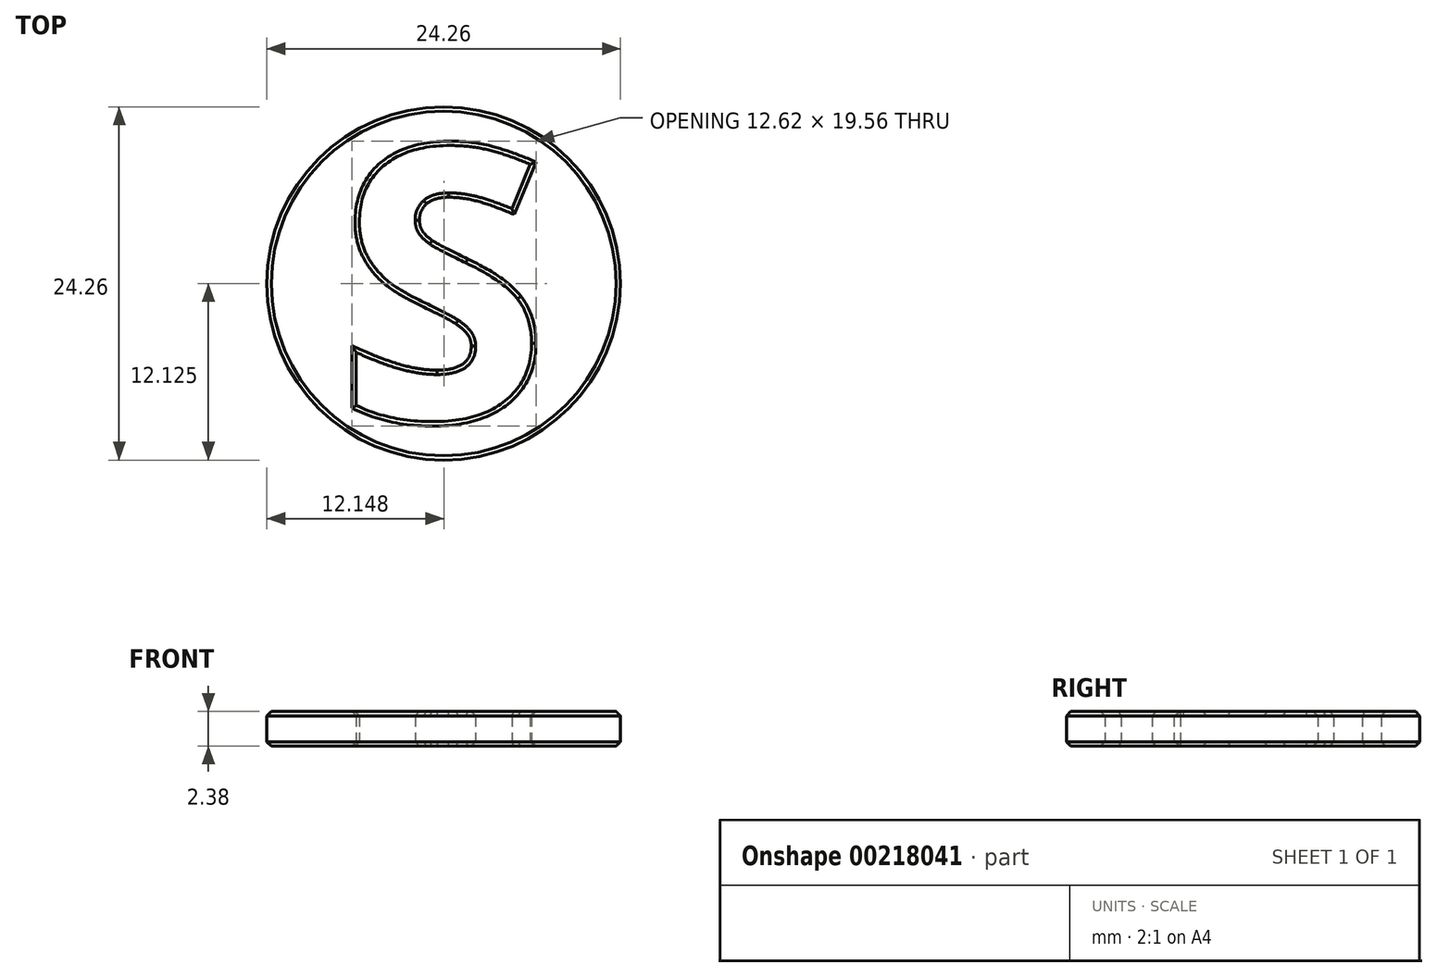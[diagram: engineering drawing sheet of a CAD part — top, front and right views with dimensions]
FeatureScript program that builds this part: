
annotation { "Feature Type Name" : "Feature", "Feature Type Description" : "" }
export const myFeature = defineFeature(function(context is Context, id is Id, definition is map)
    precondition{}
    {
        {
            var Q0;
            Q0=qCreatedBy(makeId("Top.planeOp"),FACE);
            var sketch = newSketch(context, id + "F0", { "sketchPlane" : qUnion([Q0])});
            skCircle(sketch, "E0", {"center": v(0, 0) * mm, "radius": 12.12 * mm});
            skText(sketch, "E1", { "text": "S", "fontName": "OpenSans-Bold.ttf"});
            const initialGuessF0  = {"E1": [-0.00718, -0.00923, 1, 0, 0.0186]};
            skSetInitialGuess(sketch, initialGuessF0);
            skSolve(sketch);
        }
        {
            var Q0;
            Q0=makeQuery(id+"F0.imprint","IMPRINT",FACE,{"disambiguationData":[TD([[makeQuery(id+"F0.imprint","IMPRINT",EDGE,{"derivedFrom":sQuery(id+"F0.wireOp",EDGE,"E0")}),1.0]])]});
            extrude(context, id + "F1", {"entities" : qUnion([Q0]), "depth" : 2.38 * mm});
        }
        {
            var Q0;
            Q0=makeQuery(id+"F1.opExtrude","CAP_FACE",FACE,{"disambiguationData":[OSD([sQuery(id+"F0.wireOp",EDGE,"E0"),sQuery(id+"F0.wireOp",EDGE,"E1.sketch_text.stroke-0"),sQuery(id+"F0.wireOp",EDGE,"E1.sketch_text.stroke-1"),sQuery(id+"F0.wireOp",EDGE,"E1.sketch_text.stroke-2"),sQuery(id+"F0.wireOp",EDGE,"E1.sketch_text.stroke-3"),sQuery(id+"F0.wireOp",EDGE,"E1.sketch_text.stroke-4"),sQuery(id+"F0.wireOp",EDGE,"E1.sketch_text.stroke-5"),sQuery(id+"F0.wireOp",EDGE,"E1.sketch_text.stroke-6"),sQuery(id+"F0.wireOp",EDGE,"E1.sketch_text.stroke-7"),sQuery(id+"F0.wireOp",EDGE,"E1.sketch_text.stroke-8"),sQuery(id+"F0.wireOp",EDGE,"E1.sketch_text.stroke-9"),sQuery(id+"F0.wireOp",EDGE,"E1.sketch_text.stroke-10"),sQuery(id+"F0.wireOp",EDGE,"E1.sketch_text.stroke-11"),sQuery(id+"F0.wireOp",EDGE,"E1.sketch_text.stroke-12"),sQuery(id+"F0.wireOp",EDGE,"E1.sketch_text.stroke-13"),sQuery(id+"F0.wireOp",EDGE,"E1.sketch_text.stroke-14"),sQuery(id+"F0.wireOp",EDGE,"E1.sketch_text.stroke-15"),sQuery(id+"F0.wireOp",EDGE,"E1.sketch_text.stroke-16"),sQuery(id+"F0.wireOp",EDGE,"E1.sketch_text.stroke-17"),sQuery(id+"F0.wireOp",EDGE,"E1.sketch_text.stroke-18"),sQuery(id+"F0.wireOp",EDGE,"E1.sketch_text.stroke-19"),sQuery(id+"F0.wireOp",EDGE,"E1.sketch_text.stroke-20"),sQuery(id+"F0.wireOp",EDGE,"E1.sketch_text.stroke-21"),sQuery(id+"F0.wireOp",EDGE,"E1.sketch_text.stroke-22"),sQuery(id+"F0.wireOp",EDGE,"E1.sketch_text.stroke-23"),sQuery(id+"F0.wireOp",EDGE,"E1.sketch_text.stroke-24"),sQuery(id+"F0.wireOp",EDGE,"E1.sketch_text.stroke-25"),sQuery(id+"F0.wireOp",EDGE,"E1.sketch_text.stroke-26"),sQuery(id+"F0.wireOp",EDGE,"E1.sketch_text.stroke-27")])],"isStart":false});
            var Q1;
            Q1=makeQuery(id+"F1.opExtrude","CAP_FACE",FACE,{"disambiguationData":[OSD([sQuery(id+"F0.wireOp",EDGE,"E0"),sQuery(id+"F0.wireOp",EDGE,"E1.sketch_text.stroke-0"),sQuery(id+"F0.wireOp",EDGE,"E1.sketch_text.stroke-1"),sQuery(id+"F0.wireOp",EDGE,"E1.sketch_text.stroke-2"),sQuery(id+"F0.wireOp",EDGE,"E1.sketch_text.stroke-3"),sQuery(id+"F0.wireOp",EDGE,"E1.sketch_text.stroke-4"),sQuery(id+"F0.wireOp",EDGE,"E1.sketch_text.stroke-5"),sQuery(id+"F0.wireOp",EDGE,"E1.sketch_text.stroke-6"),sQuery(id+"F0.wireOp",EDGE,"E1.sketch_text.stroke-7"),sQuery(id+"F0.wireOp",EDGE,"E1.sketch_text.stroke-8"),sQuery(id+"F0.wireOp",EDGE,"E1.sketch_text.stroke-9"),sQuery(id+"F0.wireOp",EDGE,"E1.sketch_text.stroke-10"),sQuery(id+"F0.wireOp",EDGE,"E1.sketch_text.stroke-11"),sQuery(id+"F0.wireOp",EDGE,"E1.sketch_text.stroke-12"),sQuery(id+"F0.wireOp",EDGE,"E1.sketch_text.stroke-13"),sQuery(id+"F0.wireOp",EDGE,"E1.sketch_text.stroke-14"),sQuery(id+"F0.wireOp",EDGE,"E1.sketch_text.stroke-15"),sQuery(id+"F0.wireOp",EDGE,"E1.sketch_text.stroke-16"),sQuery(id+"F0.wireOp",EDGE,"E1.sketch_text.stroke-17"),sQuery(id+"F0.wireOp",EDGE,"E1.sketch_text.stroke-18"),sQuery(id+"F0.wireOp",EDGE,"E1.sketch_text.stroke-19"),sQuery(id+"F0.wireOp",EDGE,"E1.sketch_text.stroke-20"),sQuery(id+"F0.wireOp",EDGE,"E1.sketch_text.stroke-21"),sQuery(id+"F0.wireOp",EDGE,"E1.sketch_text.stroke-22"),sQuery(id+"F0.wireOp",EDGE,"E1.sketch_text.stroke-23"),sQuery(id+"F0.wireOp",EDGE,"E1.sketch_text.stroke-24"),sQuery(id+"F0.wireOp",EDGE,"E1.sketch_text.stroke-25"),sQuery(id+"F0.wireOp",EDGE,"E1.sketch_text.stroke-26"),sQuery(id+"F0.wireOp",EDGE,"E1.sketch_text.stroke-27")])],"isStart":true});
            chamfer(context, id + "F2", {"entities" : qUnion([Q0, Q1]), "width" : .3 * mm, "tangentPropagation" : true});
        }
    });
